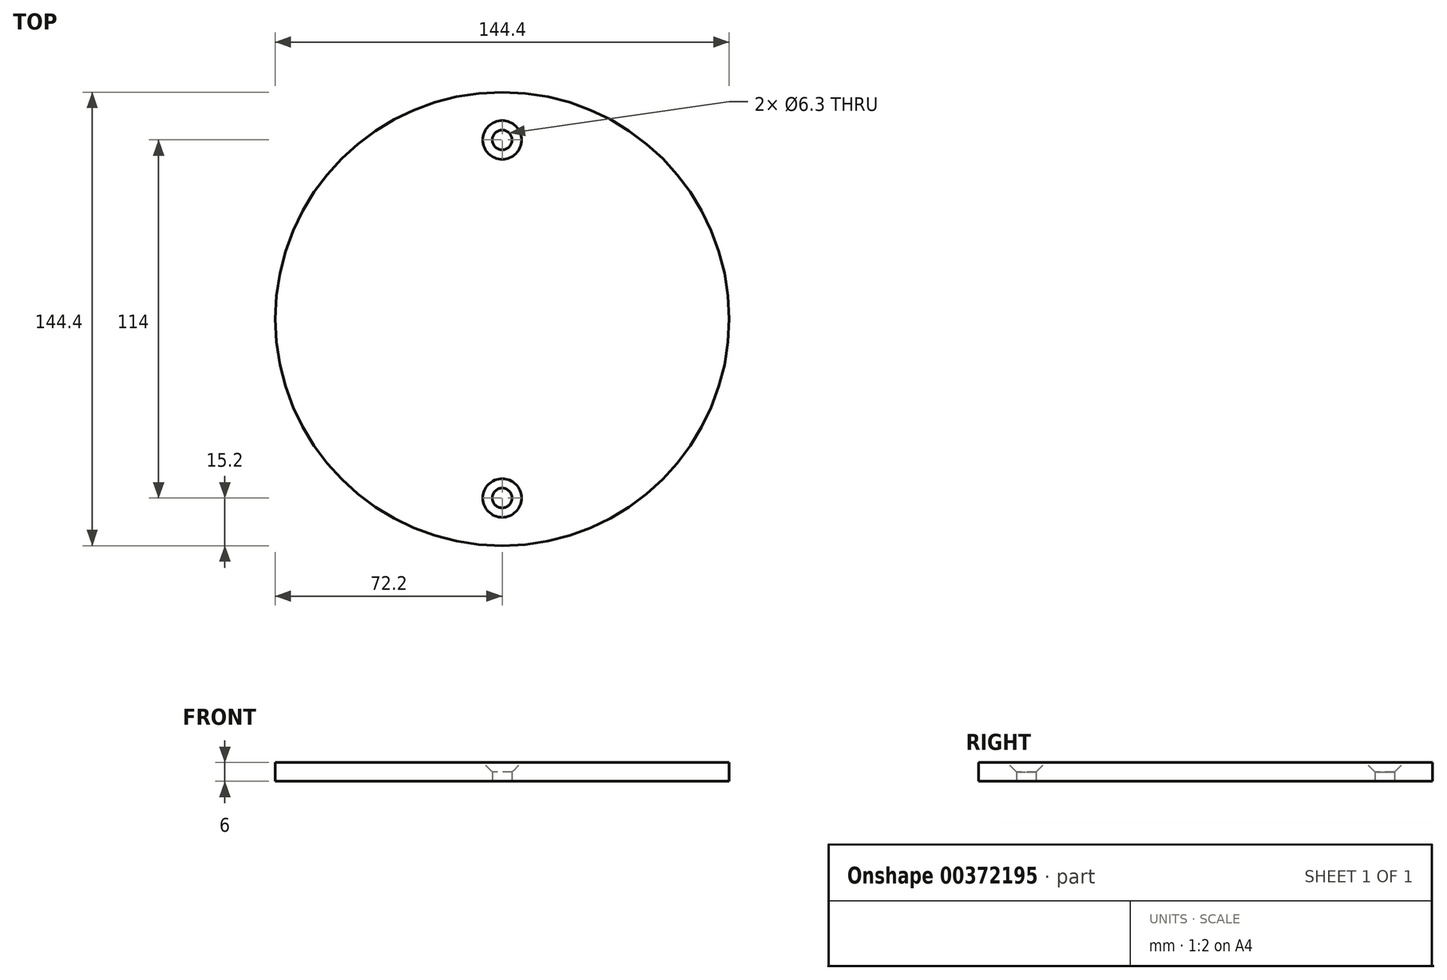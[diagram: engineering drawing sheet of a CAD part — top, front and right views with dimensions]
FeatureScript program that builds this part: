
annotation { "Feature Type Name" : "Feature", "Feature Type Description" : "" }
export const myFeature = defineFeature(function(context is Context, id is Id, definition is map)
    precondition{}
    {
        {
            var Q0;
            Q0=qCreatedBy(makeId("Top.planeOp"),FACE);
            var sketch = newSketch(context, id + "F0", { "sketchPlane" : qUnion([Q0])});
            skCircle(sketch, "E0", {"center": v(0, 0) * mm, "radius": 24.07 * mm});
            skCircle(sketch, "E1", {"center": v(0, 19) * mm, "radius": 1.05 * mm});
            skCircle(sketch, "E2", {"center": v(0, -19) * mm, "radius": 1.05 * mm});
            skSolve(sketch);
        }
        {
            var Q0;
            Q0=makeQuery(id+"F0.imprint","IMPRINT",FACE,{"disambiguationData":[TD([[makeQuery(id+"F0.imprint","IMPRINT",EDGE,{"derivedFrom":sQuery(id+"F0.wireOp",EDGE,"E0")}),1.0]])]});
            extrude(context, id + "F1", {"entities" : qUnion([Q0]), "depth" : 2 * mm});
        }
        {
            var Q0;
            Q0=makeQuery(id+"F1.opExtrude","CAP_EDGE",EDGE,{"disambiguationData":[OSD([sQuery(id+"F0.wireOp",EDGE,"E1")])],"isStart":false});
            var Q1;
            Q1=makeQuery(id+"F1.opExtrude","CAP_EDGE",EDGE,{"disambiguationData":[OSD([sQuery(id+"F0.wireOp",EDGE,"E2")])],"isStart":false});
            chamfer(context, id + "F2", {"entities" : qUnion([Q0, Q1]), "width" : 1 * mm, "tangentPropagation" : true});
        }
        {
            var Q0;
            Q0=makeQuery(id+"F1.opExtrude","SWEPT_BODY",BODY,{"disambiguationData":[OSD([sQuery(id+"F0.wireOp",EDGE,"E0"),sQuery(id+"F0.wireOp",EDGE,"E1"),sQuery(id+"F0.wireOp",EDGE,"E2")])]});
            var Q1;
            Q1=qCreatedBy(makeId("Origin.pointOp"),VERTEX);
            transform(context, id + "F3", {"entities" : qUnion([Q0]), "transformType" : TransformType.SCALE_UNIFORMLY, "scale" : 3, "makeCopy" : false, "scalePoint" : qUnion([Q1])});
        }
    });
